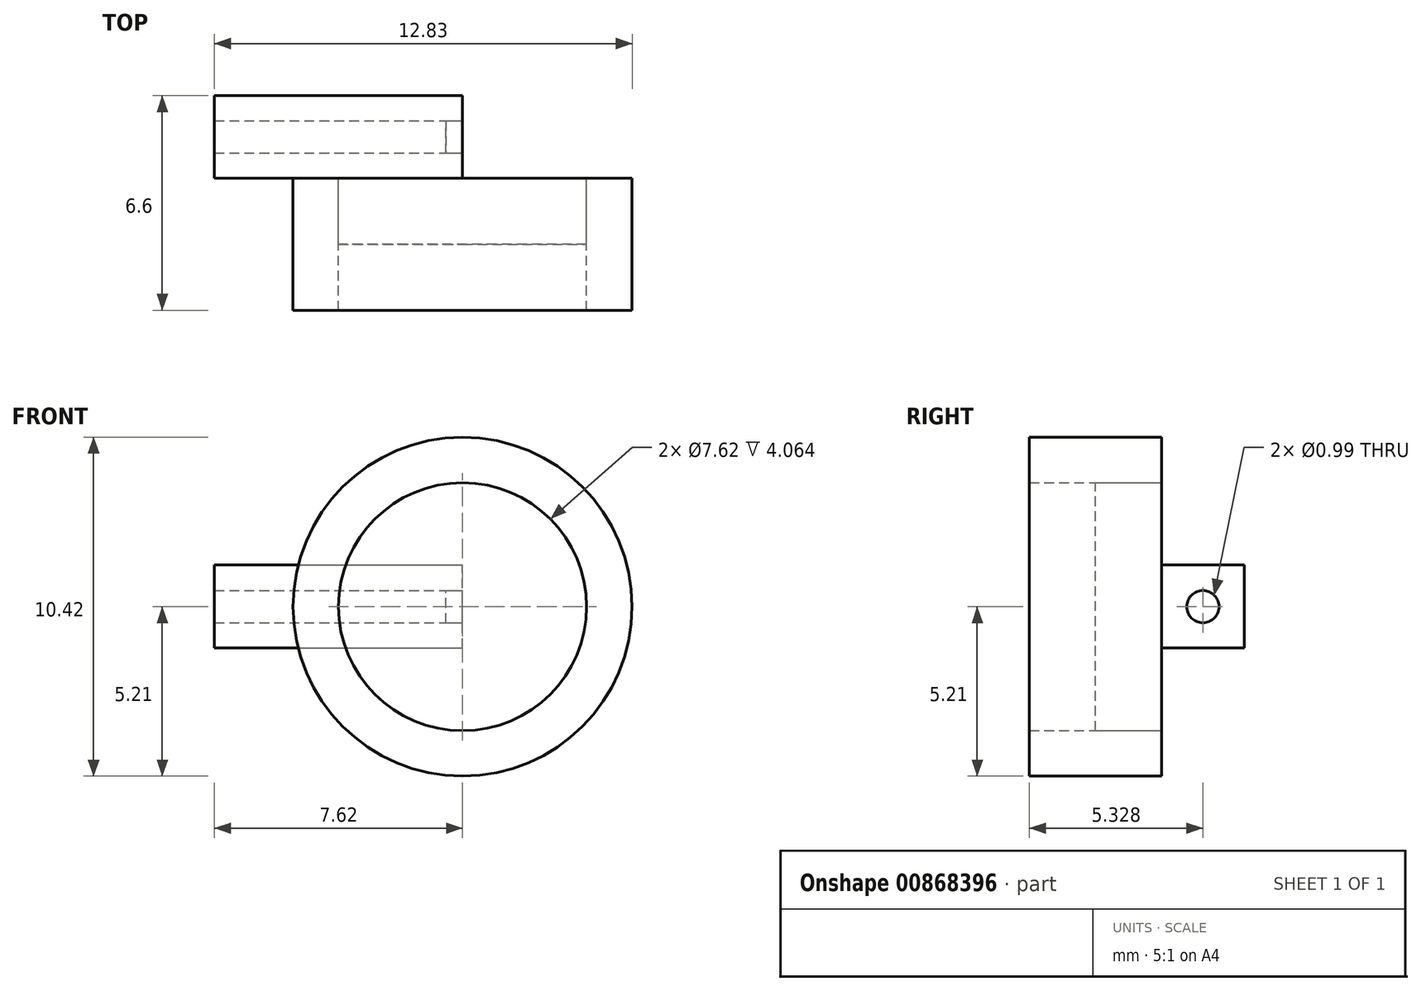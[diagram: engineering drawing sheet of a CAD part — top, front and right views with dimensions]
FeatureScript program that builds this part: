
annotation { "Feature Type Name" : "Feature", "Feature Type Description" : "" }
export const myFeature = defineFeature(function(context is Context, id is Id, definition is map)
    precondition{}
    {
        {
            var Q0;
            Q0=qCreatedBy(makeId("Front.planeOp"),FACE);
            var sketch = newSketch(context, id + "F0", { "sketchPlane" : qUnion([Q0])});
            skCircle(sketch, "E0", {"center": v(0, 0) * mm, "radius": 5.2 * mm});
            skCircle(sketch, "E1", {"center": v(0, 0) * mm, "radius": 3.81 * mm});
            skSolve(sketch);
        }
        {
            var Q0;
            Q0=makeQuery(id+"F0.imprint","IMPRINT",FACE,{"disambiguationData":[TD([[makeQuery(id+"F0.imprint","IMPRINT",EDGE,{"derivedFrom":sQuery(id+"F0.wireOp",EDGE,"E0")}),1.0]])]});
            extrude(context, id + "F1", {"entities" : qUnion([Q0]), "depth" : 4.06 * mm, "offsetDistance" : 25.4 * mm});
        }
        {
            var Q0;
            Q0=makeQuery(id+"F0.imprint","IMPRINT",FACE,{"disambiguationData":[TD([[makeQuery(id+"F0.imprint","IMPRINT",EDGE,{"derivedFrom":sQuery(id+"F0.wireOp",EDGE,"E1")}),1.0]])]});
            extrude(context, id + "F2", {"entities" : qUnion([Q0]), "depth" : 2.03 * mm, "offsetDistance" : 25.4 * mm});
        }
        {
            var Q0;
            Q0=qCreatedBy(makeId("Right.planeOp"),FACE);
            var sketch = newSketch(context, id + "F3", { "sketchPlane" : qUnion([Q0])});
            skLineSegment(sketch, "E2", {"start": v(0, 0) * mm, "end": v(0, 1.28) * mm});
            skLineSegment(sketch, "E3.bottom", {"start": v(0, 1.28) * mm, "end": v(2.54, 1.28) * mm});
            skLineSegment(sketch, "E3.top", {"start": v(0, -1.27) * mm, "end": v(2.54, -1.27) * mm});
            skLineSegment(sketch, "E3.left", {"start": v(0, 1.28) * mm, "end": v(0, -1.27) * mm});
            skLineSegment(sketch, "E3.right", {"start": v(2.54, 1.28) * mm, "end": v(2.54, -1.27) * mm});
            skCircle(sketch, "E4", {"center": v(1.27, 0) * mm, "radius": 0.5 * mm});
            skSolve(sketch);
        }
        {
            var Q0;
            Q0=makeQuery(id+"F3.imprint","IMPRINT",FACE,{"disambiguationData":[TD([[makeQuery(id+"F3.imprint","IMPRINT",EDGE,{"derivedFrom":sQuery(id+"F3.wireOp",EDGE,"E4")}),1.0]])]});
            extrude(context, id + "F4", {"entities" : qUnion([Q0]), "oppositeDirection" : true, "depth" : 0.5 * mm, "offsetDistance" : 25.4 * mm});
        }
        {
            var Q0;
            {var subQ1=sQuery(id+"F3.wireOp",EDGE,"E3.bottom");Q0=makeQuery(id+"F3.imprint","IMPRINT",FACE,{"disambiguationData":[TD([[makeQuery(id+"F3.imprint","IMPRINT",EDGE,{"derivedFrom":subQ1}),-1.0]])]});}
            extrude(context, id + "F5", {"entities" : qUnion([Q0]), "oppositeDirection" : true, "depth" : 7.62 * mm, "offsetDistance" : 25.4 * mm});
        }
    });
